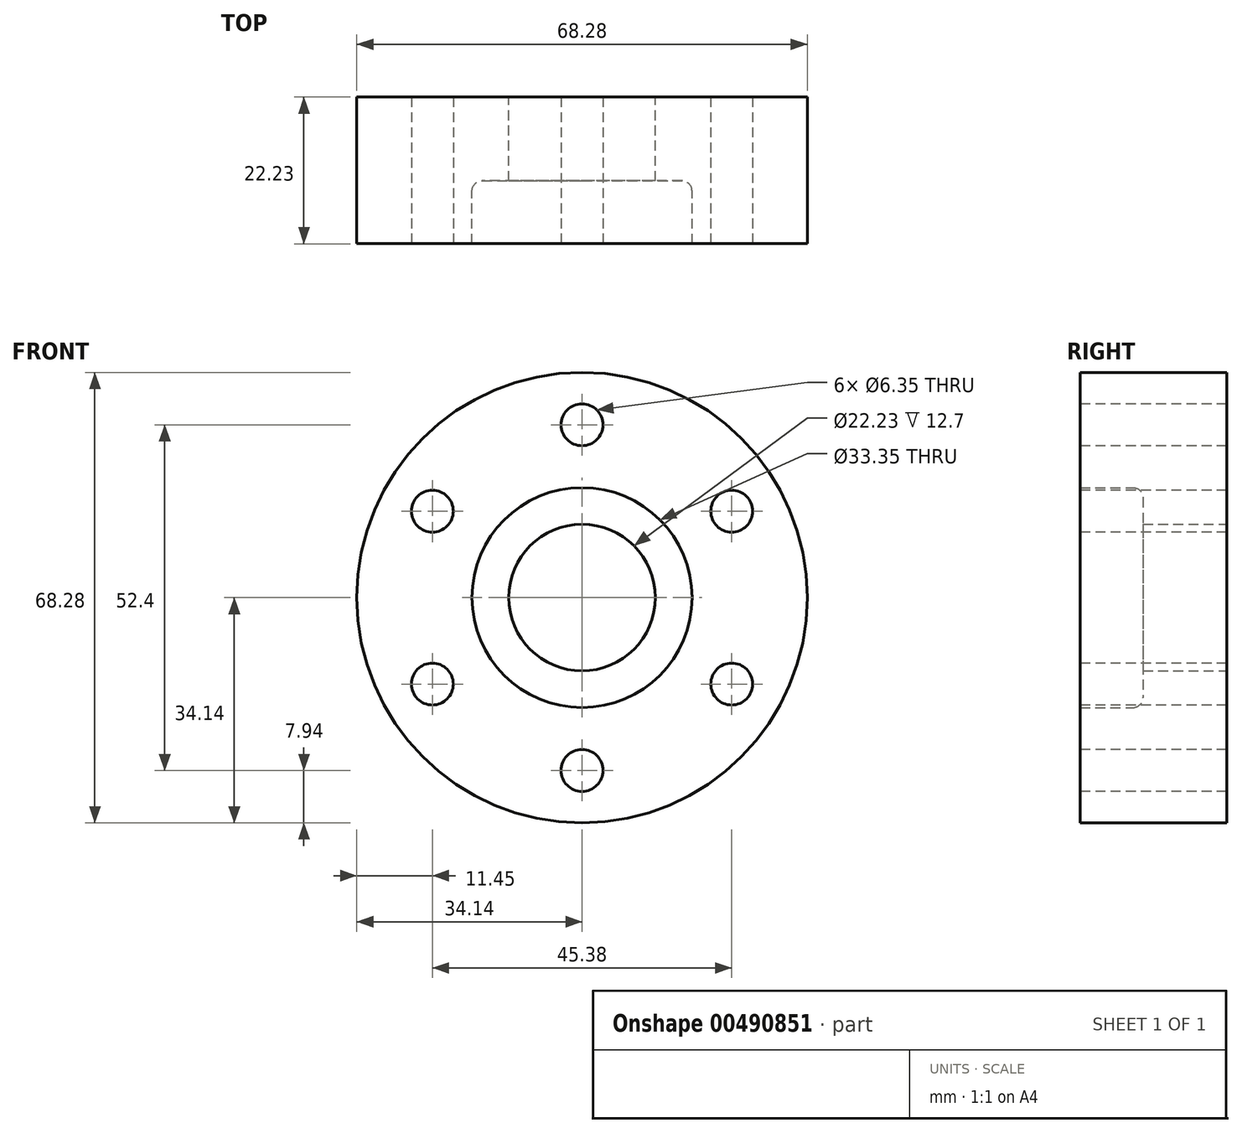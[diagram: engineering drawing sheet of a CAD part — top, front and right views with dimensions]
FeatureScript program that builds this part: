
annotation { "Feature Type Name" : "Feature", "Feature Type Description" : "" }
export const myFeature = defineFeature(function(context is Context, id is Id, definition is map)
    precondition{}
    {
        {
            var Q0;
            Q0=qCreatedBy(makeId("Right.planeOp"),FACE);
            var sketch = newSketch(context, id + "F0", { "sketchPlane" : qUnion([Q0])});
            skLineSegment(sketch, "E0", {"start": v(0, 0) * mm, "end": v(-18.55, 0) * mm, "construction": true});
            skLineSegment(sketch, "E1", {"start": v(0, 11.11) * mm, "end": v(-12.7, 11.11) * mm});
            skLineSegment(sketch, "E2", {"start": v(-12.7, 11.11) * mm, "end": v(-12.7, 16.68) * mm});
            skLineSegment(sketch, "E3", {"start": v(-12.7, 16.68) * mm, "end": v(-22.23, 16.68) * mm});
            skLineSegment(sketch, "E4", {"start": v(-22.23, 16.68) * mm, "end": v(-22.23, 34.14) * mm});
            skLineSegment(sketch, "E5", {"start": v(-22.23, 34.14) * mm, "end": v(0, 34.14) * mm});
            skLineSegment(sketch, "E6", {"start": v(0, 34.14) * mm, "end": v(0, 11.11) * mm});
            skSolve(sketch);
        }
        {
            var Q0;
            Q0 = qSketchRegion(id + "F0", true);
            var Q1;
            Q1=sQuery(id+"F0.wireOp",EDGE,"E0");
            revolve(context, id + "F1", {"entities" : qUnion([Q0]), "axis" : qUnion([Q1]), "revolveType" : RevolveType.FULL});
        }
        {
            var Q0;
            Q0=makeQuery(id+"F1.opRevolve","SWEPT_EDGE",EDGE,{"disambiguationData":[OSD([sQuery(id+"F0.wireOp",EDGE,"E2"),sQuery(id+"F0.wireOp",EDGE,"E3")])]});
            fillet(context, id + "F2", {"entities" : qUnion([Q0]), "radius" : 1.52 * mm, "tangentPropagation" : true, "allowEdgeOverflow" : false});
        }
        {
            var Q0;
            Q0=makeQuery(id+"F1.opRevolve","SWEPT_FACE",FACE,{"disambiguationData":[OSD([sQuery(id+"F0.wireOp",EDGE,"E4")])]});
            var sketch = newSketch(context, id + "F3", { "sketchPlane" : qUnion([Q0])});
            skCircle(sketch, "E7", {"center": v(0, 0) * mm, "radius": 26.2 * mm, "construction": true});
            skCircle(sketch, "E8", {"center": v(0, -26.2) * mm, "radius": 3.18 * mm});
            skSolve(sketch);
        }
        {
            var Q0;
            Q0=makeQuery(id+"F3.imprint","IMPRINT",FACE,{"disambiguationData":[TD([[makeQuery(id+"F3.imprint","IMPRINT",EDGE,{"derivedFrom":sQuery(id+"F3.wireOp",EDGE,"E8")}),1.0]])]});
            extrude(context, id + "F4", {"entities" : qUnion([Q0]), "operationType" : NewBodyOperationType.REMOVE, "endBound" : BoundingType.THROUGH_ALL, "oppositeDirection" : true, "depth" : 25 * mm});
        }
        {
            var Q0;
            Q0=makeQuery(id+"F4.boolean.opBoolean","COPY",FACE,{"derivedFrom":makeQuery(id+"F4.opExtrude","SWEPT_FACE",FACE,{"disambiguationData":[OSD([sQuery(id+"F3.wireOp",EDGE,"E8")])]})});
            var Q1;
            Q1=sQuery(id+"F3.wireOp",EDGE,"E7");
            circularPattern(context, id + "F5", {"patternType" : PatternType.FACE, "faces" : qUnion([Q0]), "axis" : qUnion([Q1]), "angle" : 360 * degree, "instanceCount" : 6, "equalSpace" : true});
        }
    });
